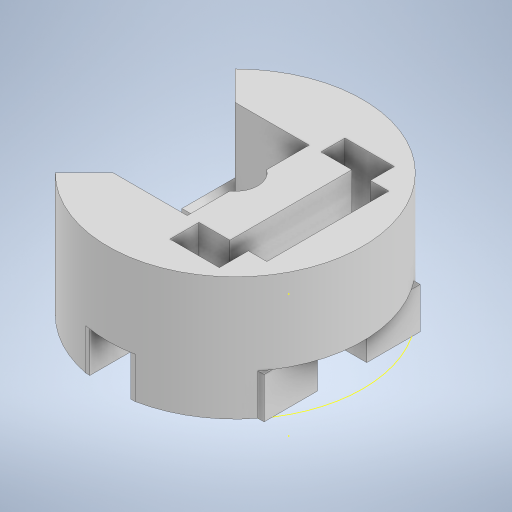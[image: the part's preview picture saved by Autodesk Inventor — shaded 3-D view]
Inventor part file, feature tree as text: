
AUTODESK INVENTOR PART (.ipt)
format: ipt  version: 2023 (Build 270158000, 158)  size: 669,184 bytes
history: native  units: in
note: dims shown in document units (in); Inventor stores cm internally (conversion verified against a paired STEP export)
features: sketch x15, extrude x12
ambient origin geometry x8: Origin, YZ Plane, XZ Plane, XY Plane, X Axis, Y Axis, Z Axis, Center Point
bodies: Body1 (feature_tree)
feature tree (27):
  extrude  "Extrusion2"  Depth=0.748in
  extrude  "Extrusion3"  Depth=0.748in
  extrude  "Extrusion4"  Depth=0.748in
  sketch  "Sketch8"  dims[d19=1.2598in d20=0.2657in]
  sketch  "Sketch9"  dims[d21=1.2598in d22=0.2657in]
  extrude  "Extrusion5"  Depth=1.2598in
  extrude  "Extrusion6"  Depth=1.2598in
  sketch  "Sketch12"  dims[d28=135.0deg d29=135.0deg]
  extrude  "Extrusion8"  Depth=0.0787in
  extrude  "Extrusion9"  Depth=0.1969in
  extrude  "Extrusion12"  TaperAngle=135.0deg  [1 undecoded]
  sketch  "Sketch19"  dims[d38=0.2362in d39=0.2362in]
  sketch  "Sketch20"  dims[d40=0.5118in]
  extrude  "Extrusion13"  Depth=0.3937in TaperAngle=0.0deg
  extrude  "Extrusion14"  Depth=0.2165in
  sketch  "Sketch23"  dims[d41=0.2362in]
  extrude  "Extrusion15"  Depth=0.3937in
  extrude  "Extrusion16"  Depth=0.2362in
  sketch  "Sketch5"  dims[d13=1.2598in d14=0.748in]
  sketch  "Sketch6"  dims[d15=0.5118in d16=0.748in]
  sketch  "Sketch7"  dims[d17=0.5118in d18=0.748in]
  sketch  "Sketch10"  dims[d23=0.315in d24=0.0787in]
  sketch  "Sketch11"  dims[d25=0.1969in d26=0.0in d27=1.2205in]
  sketch  "Sketch14"  dims[d30=0.3937in d31=0.3937in d32=0.0in]
  sketch  "Sketch16"  dims[d33=0.0787in d34=0.2165in]
  sketch  "Sketch18"  dims[d35=0.3937in d36=0.0in d37=0.5118in]
  sketch  "Sketch24"  dims[d42=0.5118in d43=0.2362in d45=0.1969in d46=0.0in d47=0.2756in d48=0.1969in d49=0.0in d58=0.1181in d59=0.0in d67=0.2559in d68=0.0in d79=0.3543in d80=0.1772in d81=0.3937in d82=0.0in d83=0.0197in d84=0.0in d85=0.0197in d86=0.0in d87=0.0197in d88=0.0in d89=0.0197in d90=0.0in d50=0.0344in d60=0.0197in d61=0.0344in d69=0.0197in d70=0.0344in]
note: 1 required parameter value undecoded (feature->parameter linkage not recoverable at this tier; creation-order binding heuristic only, values carry confidence <= 0.55)
